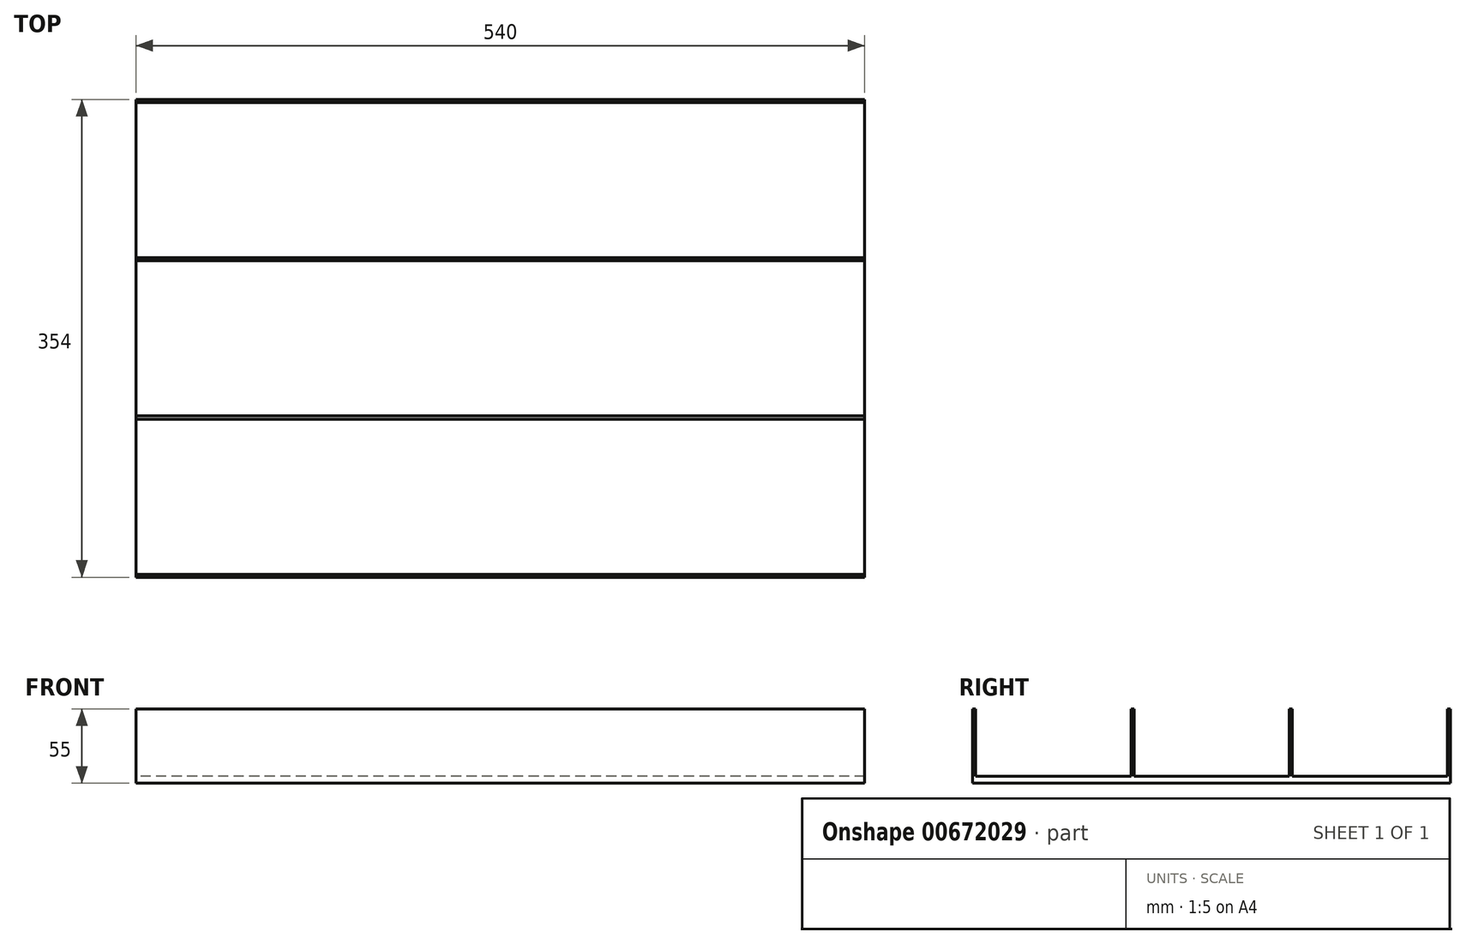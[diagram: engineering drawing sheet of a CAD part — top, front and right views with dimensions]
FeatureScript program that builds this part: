
annotation { "Feature Type Name" : "Feature", "Feature Type Description" : "" }
export const myFeature = defineFeature(function(context is Context, id is Id, definition is map)
    precondition{}
    {
        {
            var Q0;
            Q0=qCreatedBy(makeId("Right.planeOp"),FACE);
            var sketch = newSketch(context, id + "F0", { "sketchPlane" : qUnion([Q0])});
            skLineSegment(sketch, "E0", {"start": v(0, 24.25) * mm, "end": v(0, -16.38) * mm, "construction": true});
            skLineSegment(sketch, "E1", {"start": v(0, 0) * mm, "end": v(-57.5, 0) * mm});
            skLineSegment(sketch, "E2", {"start": v(-57.5, 0) * mm, "end": v(-57.5, 50) * mm});
            skLineSegment(sketch, "E3", {"start": v(-57.5, 50) * mm, "end": v(-59.75, 50) * mm});
            skLineSegment(sketch, "E4", {"start": v(-59.75, 50) * mm, "end": v(-59.75, 0) * mm});
            skLineSegment(sketch, "E5", {"start": v(-59.75, 0) * mm, "end": v(-174.75, 0) * mm});
            skLineSegment(sketch, "E6", {"start": v(-174.75, 0) * mm, "end": v(-174.75, 50) * mm});
            skLineSegment(sketch, "E7", {"start": v(-174.75, 50) * mm, "end": v(-177, 50) * mm});
            skLineSegment(sketch, "E8", {"start": v(-177, 50) * mm, "end": v(-177, -5) * mm});
            skLineSegment(sketch, "E9", {"start": v(-177, -5) * mm, "end": v(0, -5) * mm});
            skLineSegment(sketch, "E10.MirrorCS", {"start": v(57.5, 50) * mm, "end": v(59.75, 50) * mm});
            skLineSegment(sketch, "E11.MirrorCS", {"start": v(174.75, 50) * mm, "end": v(177, 50) * mm});
            skLineSegment(sketch, "E12.MirrorCS", {"start": v(0, 0) * mm, "end": v(57.5, 0) * mm});
            skLineSegment(sketch, "E13.MirrorCS", {"start": v(57.5, 0) * mm, "end": v(57.5, 50) * mm});
            skLineSegment(sketch, "E14.MirrorCS", {"start": v(59.75, 0) * mm, "end": v(174.75, 0) * mm});
            skLineSegment(sketch, "E15.MirrorCS", {"start": v(177, -5) * mm, "end": v(0, -5) * mm});
            skLineSegment(sketch, "E16.MirrorCS", {"start": v(177, 50) * mm, "end": v(177, -5) * mm});
            skLineSegment(sketch, "E17.MirrorCS", {"start": v(59.75, 50) * mm, "end": v(59.75, 0) * mm});
            skLineSegment(sketch, "E18.MirrorCS", {"start": v(174.75, 0) * mm, "end": v(174.75, 50) * mm});
            skSolve(sketch);
        }
        {
            var Q0;
            Q0=makeQuery(id+"F0.imprint","IMPRINT",FACE,{"disambiguationData":[TD([[makeQuery(id+"F0.imprint","IMPRINT",EDGE,{"derivedFrom":sQuery(id+"F0.wireOp",EDGE,"E1")}),1.0]])]});
            extrude(context, id + "F1", {"entities" : qUnion([Q0]), "endBound" : BoundingType.SYMMETRIC, "depth" : 540 * mm, "offsetDistance" : 25 * mm});
        }
    });
